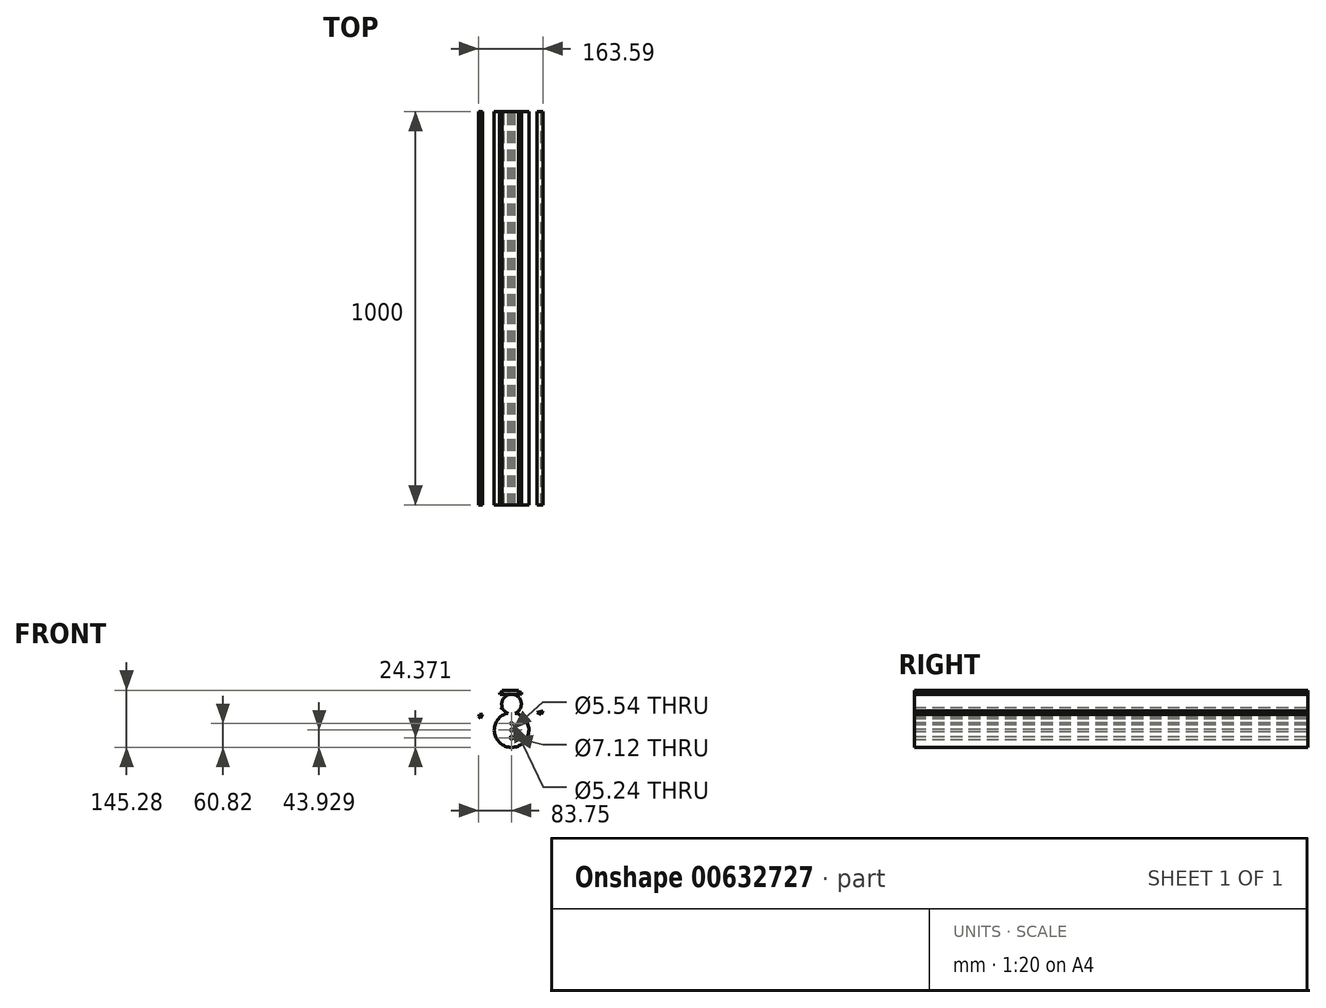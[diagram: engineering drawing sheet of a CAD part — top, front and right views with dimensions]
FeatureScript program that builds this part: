
annotation { "Feature Type Name" : "Feature", "Feature Type Description" : "" }
export const myFeature = defineFeature(function(context is Context, id is Id, definition is map)
    precondition{}
    {
        {
            var Q0;
            Q0=qCreatedBy(makeId("Front.planeOp"),FACE);
            var sketch = newSketch(context, id + "F0", { "sketchPlane" : qUnion([Q0])});
            skCircle(sketch, "E0", {"center": v(0, -24.15) * mm, "radius": 43.93 * mm});
            skCircle(sketch, "E1", {"center": v(0, 41.93) * mm, "radius": 24.92 * mm});
            skCircle(sketch, "E2", {"center": v(-9.04, 46.38) * mm, "radius": 8.89 * mm});
            skCircle(sketch, "E3", {"center": v(10.52, 46.38) * mm, "radius": 9.13 * mm});
            skCircle(sketch, "E4", {"center": v(0, -7.26) * mm, "radius": 2.62 * mm});
            skCircle(sketch, "E5", {"center": v(0, -24.15) * mm, "radius": 2.77 * mm});
            skCircle(sketch, "E6", {"center": v(0, -43.7) * mm, "radius": 3.56 * mm});
            skFitSpline(sketch, "E7", {"points": [v(-13.48, 31.86) * mm, v(-7.85, 25.93) * mm], "startDerivative": vector(5.63, -5.93) * mm, "endDerivative": vector(5.63, -5.93) * mm});
            skFitSpline(sketch, "E8", {"points": [v(-7.85, 25.93) * mm, v(0, 25.93) * mm], "startDerivative": vector(7.85, 0) * mm, "endDerivative": vector(7.85, 0) * mm});
            skFitSpline(sketch, "E9", {"points": [v(0, 25.93) * mm, v(4.6, 25.93) * mm], "startDerivative": vector(4.6, 0) * mm, "endDerivative": vector(4.6, 0) * mm});
            skFitSpline(sketch, "E10", {"points": [v(4.6, 25.93) * mm, v(5.75, 27.37) * mm, v(8.15, 30.37) * mm], "startDerivative": vector(3.56, 4.45) * mm, "endDerivative": vector(3.56, 4.45) * mm});
            skLineSegment(sketch, "E11", {"start": v(-3.51, 33.94) * mm, "end": v(-27.81, 33.94) * mm});
            skLineSegment(sketch, "E12", {"start": v(-27.81, 33.94) * mm, "end": v(-19.98, 26.54) * mm});
            skLineSegment(sketch, "E13", {"start": v(-19.98, 26.54) * mm, "end": v(-3.51, 33.94) * mm});
            skLineSegment(sketch, "E14", {"start": v(0, 66.85) * mm, "end": v(-29.49, 66.85) * mm});
            skLineSegment(sketch, "E15", {"start": v(-29.49, 66.85) * mm, "end": v(-30.28, 71.54) * mm});
            skLineSegment(sketch, "E16", {"start": v(-30.28, 71.54) * mm, "end": v(-24.79, 70.73) * mm});
            skLineSegment(sketch, "E17", {"start": v(-24.79, 70.73) * mm, "end": v(-24.79, 77.2) * mm});
            skLineSegment(sketch, "E18", {"start": v(-24.79, 77.2) * mm, "end": v(18.22, 77.2) * mm});
            skLineSegment(sketch, "E19", {"start": v(18.22, 77.2) * mm, "end": v(18.22, 71.54) * mm});
            skLineSegment(sketch, "E20", {"start": v(-6.34, 67.91) * mm, "end": v(-7.85, 66.85) * mm});
            skLineSegment(sketch, "E21", {"start": v(18.22, 71.54) * mm, "end": v(25.04, 71.54) * mm});
            skLineSegment(sketch, "E22", {"start": v(25.04, 71.54) * mm, "end": v(25.04, 66.53) * mm});
            skLineSegment(sketch, "E23", {"start": v(25.04, 66.53) * mm, "end": v(-6.34, 67.91) * mm});
            skLineSegment(sketch, "E24", {"start": v(-42.52, -13.12) * mm, "end": v(-76, 10.82) * mm});
            skLineSegment(sketch, "E25", {"start": v(42.57, -13.3) * mm, "end": v(75.42, 15.56) * mm});
            skLineSegment(sketch, "E26", {"start": v(75.42, 15.56) * mm, "end": v(65.05, 20.9) * mm});
            skLineSegment(sketch, "E27", {"start": v(75.42, 15.56) * mm, "end": v(79.84, 24.16) * mm});
            skLineSegment(sketch, "E28", {"start": v(79.84, 24.16) * mm, "end": v(75.42, 15.56) * mm});
            skLineSegment(sketch, "E29", {"start": v(78.08, 15.56) * mm, "end": v(85.5, 15.56) * mm});
            skLineSegment(sketch, "E30", {"start": v(85.5, 15.56) * mm, "end": v(79.84, 24.16) * mm});
            skLineSegment(sketch, "E31", {"start": v(65.05, 20.9) * mm, "end": v(79.84, 24.16) * mm});
            skLineSegment(sketch, "E32", {"start": v(-76, 10.82) * mm, "end": v(-78.87, 5.26) * mm});
            skLineSegment(sketch, "E33", {"start": v(-78.87, 5.26) * mm, "end": v(-83.75, 10.82) * mm});
            skLineSegment(sketch, "E34", {"start": v(-83.75, 10.82) * mm, "end": v(-76, 10.82) * mm});
            skLineSegment(sketch, "E35", {"start": v(-76, 10.82) * mm, "end": v(-73.57, 15.56) * mm});
            skLineSegment(sketch, "E36", {"start": v(-73.57, 15.56) * mm, "end": v(-81.34, 15.56) * mm});
            skLineSegment(sketch, "E37", {"start": v(-81.34, 15.56) * mm, "end": v(-83.75, 10.82) * mm});
            skSolve(sketch);
        }
        {
            var Q0;
            Q0=makeQuery(id+"F0.imprint","IMPRINT",FACE,{"disambiguationData":[TD([[makeQuery(id+"F0.imprint","IMPRINT",EDGE,{"derivedFrom":sQuery(id+"F0.wireOp",EDGE,"E2")}),-1.0]])]});
            var Q1;
            {var subQ0=sQuery(id+"F0.wireOp",EDGE,"E1");var subQ1=sQuery(id+"F0.wireOp",EDGE,"E0");var subQ2=makeQuery(id+"F0.imprint","INTERSECT",VERTEX,{"disambiguationData":[OD(0.0)],"derivedFrom":[subQ1,subQ0]});Q1=makeQuery(id+"F0.imprint","IMPRINT",FACE,{"disambiguationData":[TD([[makeQuery(id+"F0.imprint","IMPRINT",EDGE,{"disambiguationData":[TD([[subQ2,-1.0]])],"derivedFrom":subQ1}),1.0]])]});}
            var Q2;
            Q2=makeQuery(id+"F0.imprint","IMPRINT",FACE,{"disambiguationData":[TD([[makeQuery(id+"F0.imprint","IMPRINT",EDGE,{"derivedFrom":sQuery(id+"F0.wireOp",EDGE,"E4")}),-1.0]])]});
            var Q3;
            {var subQ0=sQuery(id+"F0.wireOp",EDGE,"E15");Q3=makeQuery(id+"F0.imprint","IMPRINT",FACE,{"disambiguationData":[TD([[makeQuery(id+"F0.imprint","IMPRINT",EDGE,{"derivedFrom":subQ0}),-1.0]])]});}
            var Q4;
            Q4=makeQuery(id+"F0.imprint","IMPRINT",FACE,{"disambiguationData":[TD([[makeQuery(id+"F0.imprint","IMPRINT",EDGE,{"derivedFrom":sQuery(id+"F0.wireOp",EDGE,"E2")}),1.0]])]});
            var Q5;
            Q5=makeQuery(id+"F0.imprint","IMPRINT",FACE,{"disambiguationData":[TD([[makeQuery(id+"F0.imprint","IMPRINT",EDGE,{"derivedFrom":sQuery(id+"F0.wireOp",EDGE,"E3")}),1.0]])]});
            var Q6;
            {var subQ3=sQuery(id+"F0.wireOp",EDGE,"E13");var subQ6=makeQuery(id+"F0.imprint","IMPRINT",VERTEX,{"derivedFrom":subQ3});Q6=makeQuery(id+"F0.imprint","IMPRINT",FACE,{"disambiguationData":[TD([[makeQuery(id+"F0.imprint","IMPRINT",EDGE,{"disambiguationData":[TD([[subQ6,1.0]])],"derivedFrom":subQ3}),1.0]])]});}
            var Q7;
            {var subQ5=sQuery(id+"F0.wireOp",EDGE,"E12");Q7=makeQuery(id+"F0.imprint","IMPRINT",FACE,{"disambiguationData":[TD([[makeQuery(id+"F0.imprint","IMPRINT",EDGE,{"derivedFrom":subQ5}),1.0]])]});}
            var Q8;
            Q8=makeQuery(id+"F0.imprint","IMPRINT",FACE,{"disambiguationData":[TD([[makeQuery(id+"F0.imprint","IMPRINT",EDGE,{"derivedFrom":sQuery(id+"F0.wireOp",EDGE,"E26")}),-1.0]])]});
            var Q9;
            Q9=makeQuery(id+"F0.imprint","IMPRINT",FACE,{"disambiguationData":[TD([[makeQuery(id+"F0.imprint","IMPRINT",EDGE,{"derivedFrom":sQuery(id+"F0.wireOp",EDGE,"E34")}),1.0]])]});
            var Q10;
            Q10=makeQuery(id+"F0.imprint","IMPRINT",FACE,{"disambiguationData":[TD([[makeQuery(id+"F0.imprint","IMPRINT",EDGE,{"derivedFrom":sQuery(id+"F0.wireOp",EDGE,"E32")}),-1.0]])]});
            extrude(context, id + "F1", {"entities" : qUnion([Q0, Q1, Q2, Q3, Q4, Q5, Q6, Q7, Q8, Q9, Q10]), "depth" : 1000 * mm, "offsetDistance" : 25 * mm});
        }
    });
